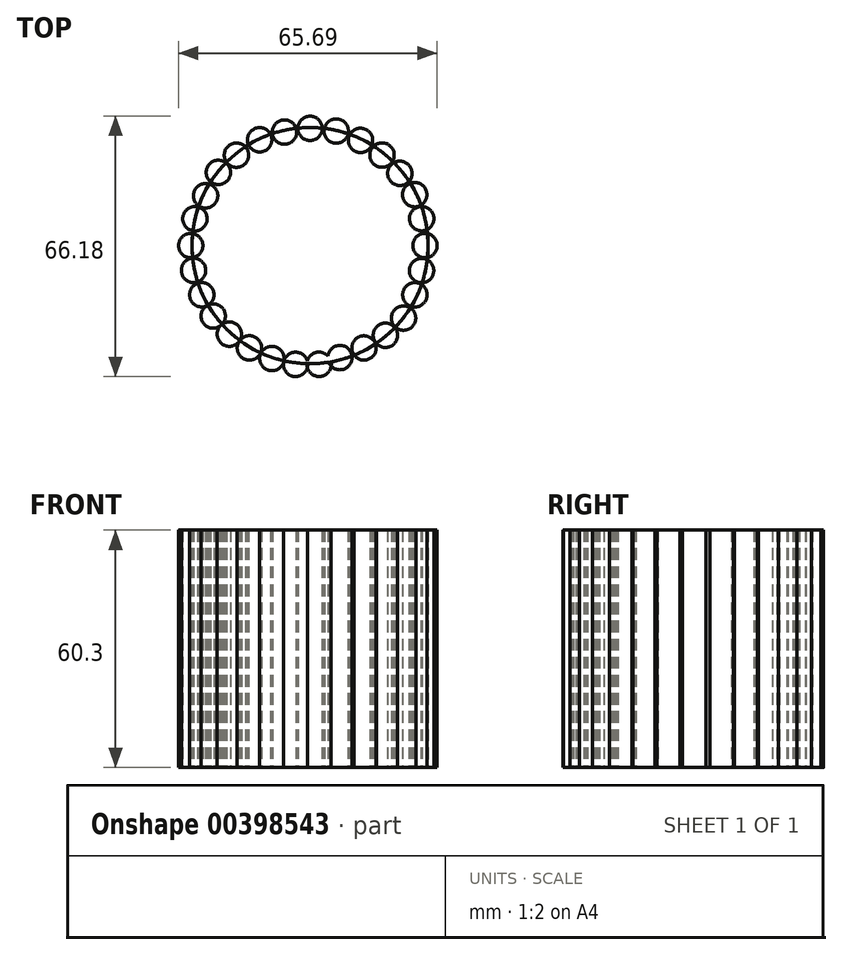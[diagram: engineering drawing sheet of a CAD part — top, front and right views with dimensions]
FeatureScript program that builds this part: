
annotation { "Feature Type Name" : "Feature", "Feature Type Description" : "" }
export const myFeature = defineFeature(function(context is Context, id is Id, definition is map)
    precondition{}
    {
        {
            var Q0;
            Q0=qCreatedBy(makeId("Top.planeOp"),FACE);
            var sketch = newSketch(context, id + "F0", { "sketchPlane" : qUnion([Q0])});
            skCircle(sketch, "E0", {"center": v(0, 0) * mm, "radius": 30 * mm});
            skSolve(sketch);
        }
        {
            var Q0;
            Q0=makeQuery(id+"F0.imprint","IMPRINT",FACE,{"disambiguationData":[TD([[makeQuery(id+"F0.imprint","IMPRINT",EDGE,{"derivedFrom":sQuery(id+"F0.wireOp",EDGE,"E0")}),1.0]])]});
            var sketch = newSketch(context, id + "F1", { "sketchPlane" : qUnion([Q0])});
            skCircle(sketch, "E1", {"center": v(-18.7, 22.97) * mm, "radius": 3.1 * mm});
            skCircle(sketch, "E2", {"center": v(-12.8, 26.88) * mm, "radius": 3.1 * mm});
            skCircle(sketch, "E3", {"center": v(-6.5, 28.84) * mm, "radius": 3.1 * mm});
            skCircle(sketch, "E4", {"center": v(0, 29.8) * mm, "radius": 3.1 * mm});
            skCircle(sketch, "E5", {"center": v(6.65, 29.1) * mm, "radius": 3.1 * mm});
            skCircle(sketch, "E6", {"center": v(12.83, 26.72) * mm, "radius": 3.1 * mm});
            skCircle(sketch, "E7", {"center": v(18.28, 23) * mm, "radius": 3.1 * mm});
            skCircle(sketch, "E8", {"center": v(22.82, 18.35) * mm, "radius": 3.1 * mm});
            skCircle(sketch, "E9", {"center": v(26.6, 12.94) * mm, "radius": 3.1 * mm});
            skCircle(sketch, "E10", {"center": v(28.36, 6.83) * mm, "radius": 3.1 * mm});
            skCircle(sketch, "E11", {"center": v(29.2, 0) * mm, "radius": 3.1 * mm});
            skCircle(sketch, "E12", {"center": v(28.34, -6.36) * mm, "radius": 3.1 * mm});
            skCircle(sketch, "E13", {"center": v(26.63, -12.5) * mm, "radius": 3.1 * mm});
            skCircle(sketch, "E14", {"center": v(23.77, -18.42) * mm, "radius": 3.1 * mm});
            skCircle(sketch, "E15", {"center": v(19.15, -22.78) * mm, "radius": 3.1 * mm});
            skCircle(sketch, "E16", {"center": v(-23.29, 18.6) * mm, "radius": 3.1 * mm});
            skCircle(sketch, "E17", {"center": v(-26.53, 12.65) * mm, "radius": 3.1 * mm});
            skCircle(sketch, "E18", {"center": v(-29.25, 6.82) * mm, "radius": 3.1 * mm});
            skCircle(sketch, "E19", {"center": v(-30.3, 0) * mm, "radius": 3.1 * mm});
            skCircle(sketch, "E20", {"center": v(-29.6, -6.3) * mm, "radius": 3.1 * mm});
            skCircle(sketch, "E21", {"center": v(-27.5, -12.5) * mm, "radius": 3.1 * mm});
            skCircle(sketch, "E22", {"center": v(-24.6, -17.9) * mm, "radius": 3.1 * mm});
            skCircle(sketch, "E23", {"center": v(-20.5, -22.5) * mm, "radius": 3.1 * mm});
            skCircle(sketch, "E24", {"center": v(13.7, -26) * mm, "radius": 3.1 * mm});
            skCircle(sketch, "E25", {"center": v(-15.4, -26) * mm, "radius": 3.1 * mm});
            skCircle(sketch, "E26", {"center": v(7.6, -28.46) * mm, "radius": 3.1 * mm});
            skCircle(sketch, "E27", {"center": v(-9.7, -28.7) * mm, "radius": 3.1 * mm});
            skCircle(sketch, "E28", {"center": v(-3.66, -30.18) * mm, "radius": 3.1 * mm});
            skCircle(sketch, "E29", {"center": v(2.3, -30.16) * mm, "radius": 3.1 * mm});
            skSolve(sketch);
        }
        {
            var Q0;
            {var subQ1=makeQuery(id+"F0.imprint","IMPRINT",EDGE,{"derivedFrom":sQuery(id+"F0.wireOp",EDGE,"E0")});var subQ36=sQuery(id+"F1.wireOp",EDGE,"E1");var subQ62=makeQuery(id+"F1.imprint","INTERSECT",VERTEX,{"disambiguationData":[OD(0.0)],"derivedFrom":[subQ1,subQ36]});Q0=makeQuery(id+"F1.imprint","IMPRINT",FACE,{"disambiguationData":[TD([[makeQuery(id+"F1.imprint","IMPRINT",EDGE,{"disambiguationData":[TD([[subQ62,-1.0]])],"derivedFrom":subQ36}),-1.0]])]});}
            var Q1;
            {var subQ0=sQuery(id+"F1.wireOp",EDGE,"E13");var subQ1=makeQuery(id+"F0.imprint","IMPRINT",EDGE,{"derivedFrom":sQuery(id+"F0.wireOp",EDGE,"E0")});var subQ2=makeQuery(id+"F1.imprint","INTERSECT",VERTEX,{"disambiguationData":[OD(0.0)],"derivedFrom":[subQ1,subQ0]});Q1=makeQuery(id+"F1.imprint","IMPRINT",FACE,{"disambiguationData":[TD([[makeQuery(id+"F1.imprint","IMPRINT",EDGE,{"disambiguationData":[TD([[subQ2,-1.0]])],"derivedFrom":subQ0}),1.0]])]});}
            var Q2;
            {var subQ0=sQuery(id+"F1.wireOp",EDGE,"E14");var subQ1=makeQuery(id+"F0.imprint","IMPRINT",EDGE,{"derivedFrom":sQuery(id+"F0.wireOp",EDGE,"E0")});var subQ2=makeQuery(id+"F1.imprint","INTERSECT",VERTEX,{"disambiguationData":[OD(0.0)],"derivedFrom":[subQ1,subQ0]});Q2=makeQuery(id+"F1.imprint","IMPRINT",FACE,{"disambiguationData":[TD([[makeQuery(id+"F1.imprint","IMPRINT",EDGE,{"disambiguationData":[TD([[subQ2,-1.0]])],"derivedFrom":subQ0}),1.0]])]});}
            var Q3;
            Q3=makeQuery(id+"F0.imprint","IMPRINT",FACE,{"disambiguationData":[TD([[makeQuery(id+"F0.imprint","IMPRINT",EDGE,{"derivedFrom":sQuery(id+"F0.wireOp",EDGE,"E0")}),1.0]])]});
            var Q4;
            {var subQ0=sQuery(id+"F1.wireOp",EDGE,"E12");var subQ1=makeQuery(id+"F0.imprint","IMPRINT",EDGE,{"derivedFrom":sQuery(id+"F0.wireOp",EDGE,"E0")});var subQ2=makeQuery(id+"F1.imprint","INTERSECT",VERTEX,{"disambiguationData":[OD(0.0)],"derivedFrom":[subQ1,subQ0]});Q4=makeQuery(id+"F1.imprint","IMPRINT",FACE,{"disambiguationData":[TD([[makeQuery(id+"F1.imprint","IMPRINT",EDGE,{"disambiguationData":[TD([[subQ2,-1.0]])],"derivedFrom":subQ0}),1.0]])]});}
            var Q5;
            {var subQ0=sQuery(id+"F1.wireOp",EDGE,"E11");var subQ1=makeQuery(id+"F0.imprint","IMPRINT",EDGE,{"derivedFrom":sQuery(id+"F0.wireOp",EDGE,"E0")});var subQ2=makeQuery(id+"F1.imprint","INTERSECT",VERTEX,{"disambiguationData":[OD(0.0)],"derivedFrom":[subQ1,subQ0]});Q5=makeQuery(id+"F1.imprint","IMPRINT",FACE,{"disambiguationData":[TD([[makeQuery(id+"F1.imprint","IMPRINT",EDGE,{"disambiguationData":[TD([[subQ2,-1.0]])],"derivedFrom":subQ0}),1.0]])]});}
            var Q6;
            {var subQ0=sQuery(id+"F1.wireOp",EDGE,"E10");var subQ1=makeQuery(id+"F0.imprint","IMPRINT",EDGE,{"derivedFrom":sQuery(id+"F0.wireOp",EDGE,"E0")});var subQ2=makeQuery(id+"F1.imprint","INTERSECT",VERTEX,{"disambiguationData":[OD(0.0)],"derivedFrom":[subQ1,subQ0]});Q6=makeQuery(id+"F1.imprint","IMPRINT",FACE,{"disambiguationData":[TD([[makeQuery(id+"F1.imprint","IMPRINT",EDGE,{"disambiguationData":[TD([[subQ2,-1.0]])],"derivedFrom":subQ0}),1.0]])]});}
            var Q7;
            {var subQ0=sQuery(id+"F1.wireOp",EDGE,"E9");var subQ1=makeQuery(id+"F0.imprint","IMPRINT",EDGE,{"derivedFrom":sQuery(id+"F0.wireOp",EDGE,"E0")});var subQ2=makeQuery(id+"F1.imprint","INTERSECT",VERTEX,{"disambiguationData":[OD(0.0)],"derivedFrom":[subQ1,subQ0]});Q7=makeQuery(id+"F1.imprint","IMPRINT",FACE,{"disambiguationData":[TD([[makeQuery(id+"F1.imprint","IMPRINT",EDGE,{"disambiguationData":[TD([[subQ2,-1.0]])],"derivedFrom":subQ0}),1.0]])]});}
            var Q8;
            {var subQ0=sQuery(id+"F1.wireOp",EDGE,"E8");var subQ1=makeQuery(id+"F0.imprint","IMPRINT",EDGE,{"derivedFrom":sQuery(id+"F0.wireOp",EDGE,"E0")});var subQ2=makeQuery(id+"F1.imprint","INTERSECT",VERTEX,{"disambiguationData":[OD(0.0)],"derivedFrom":[subQ1,subQ0]});Q8=makeQuery(id+"F1.imprint","IMPRINT",FACE,{"disambiguationData":[TD([[makeQuery(id+"F1.imprint","IMPRINT",EDGE,{"disambiguationData":[TD([[subQ2,-1.0]])],"derivedFrom":subQ0}),1.0]])]});}
            var Q9;
            {var subQ0=sQuery(id+"F1.wireOp",EDGE,"E7");var subQ1=makeQuery(id+"F0.imprint","IMPRINT",EDGE,{"derivedFrom":sQuery(id+"F0.wireOp",EDGE,"E0")});var subQ2=makeQuery(id+"F1.imprint","INTERSECT",VERTEX,{"disambiguationData":[OD(0.0)],"derivedFrom":[subQ1,subQ0]});Q9=makeQuery(id+"F1.imprint","IMPRINT",FACE,{"disambiguationData":[TD([[makeQuery(id+"F1.imprint","IMPRINT",EDGE,{"disambiguationData":[TD([[subQ2,-1.0]])],"derivedFrom":subQ0}),1.0]])]});}
            var Q10;
            {var subQ0=sQuery(id+"F1.wireOp",EDGE,"E6");var subQ1=makeQuery(id+"F0.imprint","IMPRINT",EDGE,{"derivedFrom":sQuery(id+"F0.wireOp",EDGE,"E0")});var subQ2=makeQuery(id+"F1.imprint","INTERSECT",VERTEX,{"disambiguationData":[OD(0.0)],"derivedFrom":[subQ1,subQ0]});Q10=makeQuery(id+"F1.imprint","IMPRINT",FACE,{"disambiguationData":[TD([[makeQuery(id+"F1.imprint","IMPRINT",EDGE,{"disambiguationData":[TD([[subQ2,1.0]])],"derivedFrom":subQ0}),1.0]])]});}
            var Q11;
            {var subQ0=sQuery(id+"F1.wireOp",EDGE,"E5");var subQ1=makeQuery(id+"F0.imprint","IMPRINT",EDGE,{"derivedFrom":sQuery(id+"F0.wireOp",EDGE,"E0")});var subQ2=makeQuery(id+"F1.imprint","INTERSECT",VERTEX,{"disambiguationData":[OD(0.0)],"derivedFrom":[subQ1,subQ0]});Q11=makeQuery(id+"F1.imprint","IMPRINT",FACE,{"disambiguationData":[TD([[makeQuery(id+"F1.imprint","IMPRINT",EDGE,{"disambiguationData":[TD([[subQ2,1.0]])],"derivedFrom":subQ0}),1.0]])]});}
            var Q12;
            {var subQ0=sQuery(id+"F1.wireOp",EDGE,"E4");var subQ1=makeQuery(id+"F0.imprint","IMPRINT",EDGE,{"derivedFrom":sQuery(id+"F0.wireOp",EDGE,"E0")});var subQ2=makeQuery(id+"F1.imprint","INTERSECT",VERTEX,{"disambiguationData":[OD(0.0)],"derivedFrom":[subQ1,subQ0]});Q12=makeQuery(id+"F1.imprint","IMPRINT",FACE,{"disambiguationData":[TD([[makeQuery(id+"F1.imprint","IMPRINT",EDGE,{"disambiguationData":[TD([[subQ2,1.0]])],"derivedFrom":subQ0}),1.0]])]});}
            var Q13;
            {var subQ0=sQuery(id+"F1.wireOp",EDGE,"E3");var subQ1=makeQuery(id+"F0.imprint","IMPRINT",EDGE,{"derivedFrom":sQuery(id+"F0.wireOp",EDGE,"E0")});var subQ2=makeQuery(id+"F1.imprint","INTERSECT",VERTEX,{"disambiguationData":[OD(0.0)],"derivedFrom":[subQ1,subQ0]});Q13=makeQuery(id+"F1.imprint","IMPRINT",FACE,{"disambiguationData":[TD([[makeQuery(id+"F1.imprint","IMPRINT",EDGE,{"disambiguationData":[TD([[subQ2,1.0]])],"derivedFrom":subQ0}),1.0]])]});}
            var Q14;
            {var subQ0=sQuery(id+"F1.wireOp",EDGE,"E2");var subQ1=makeQuery(id+"F0.imprint","IMPRINT",EDGE,{"derivedFrom":sQuery(id+"F0.wireOp",EDGE,"E0")});var subQ2=makeQuery(id+"F1.imprint","INTERSECT",VERTEX,{"disambiguationData":[OD(0.0)],"derivedFrom":[subQ1,subQ0]});Q14=makeQuery(id+"F1.imprint","IMPRINT",FACE,{"disambiguationData":[TD([[makeQuery(id+"F1.imprint","IMPRINT",EDGE,{"disambiguationData":[TD([[subQ2,1.0]])],"derivedFrom":subQ0}),1.0]])]});}
            var Q15;
            {var subQ0=sQuery(id+"F1.wireOp",EDGE,"E1");var subQ1=makeQuery(id+"F0.imprint","IMPRINT",EDGE,{"derivedFrom":sQuery(id+"F0.wireOp",EDGE,"E0")});var subQ2=makeQuery(id+"F1.imprint","INTERSECT",VERTEX,{"disambiguationData":[OD(0.0)],"derivedFrom":[subQ1,subQ0]});Q15=makeQuery(id+"F1.imprint","IMPRINT",FACE,{"disambiguationData":[TD([[makeQuery(id+"F1.imprint","IMPRINT",EDGE,{"disambiguationData":[TD([[subQ2,1.0]])],"derivedFrom":subQ0}),1.0]])]});}
            var Q16;
            {var subQ0=sQuery(id+"F1.wireOp",EDGE,"E16");var subQ1=makeQuery(id+"F0.imprint","IMPRINT",EDGE,{"derivedFrom":sQuery(id+"F0.wireOp",EDGE,"E0")});var subQ2=makeQuery(id+"F1.imprint","INTERSECT",VERTEX,{"disambiguationData":[OD(0.0)],"derivedFrom":[subQ1,subQ0]});Q16=makeQuery(id+"F1.imprint","IMPRINT",FACE,{"disambiguationData":[TD([[makeQuery(id+"F1.imprint","IMPRINT",EDGE,{"disambiguationData":[TD([[subQ2,1.0]])],"derivedFrom":subQ0}),1.0]])]});}
            var Q17;
            {var subQ0=sQuery(id+"F1.wireOp",EDGE,"E17");var subQ1=makeQuery(id+"F0.imprint","IMPRINT",EDGE,{"derivedFrom":sQuery(id+"F0.wireOp",EDGE,"E0")});var subQ2=makeQuery(id+"F1.imprint","INTERSECT",VERTEX,{"disambiguationData":[OD(0.0)],"derivedFrom":[subQ1,subQ0]});Q17=makeQuery(id+"F1.imprint","IMPRINT",FACE,{"disambiguationData":[TD([[makeQuery(id+"F1.imprint","IMPRINT",EDGE,{"disambiguationData":[TD([[subQ2,1.0]])],"derivedFrom":subQ0}),1.0]])]});}
            var Q18;
            {var subQ0=sQuery(id+"F1.wireOp",EDGE,"E18");var subQ1=makeQuery(id+"F0.imprint","IMPRINT",EDGE,{"derivedFrom":sQuery(id+"F0.wireOp",EDGE,"E0")});var subQ2=makeQuery(id+"F1.imprint","INTERSECT",VERTEX,{"disambiguationData":[OD(0.0)],"derivedFrom":[subQ1,subQ0]});Q18=makeQuery(id+"F1.imprint","IMPRINT",FACE,{"disambiguationData":[TD([[makeQuery(id+"F1.imprint","IMPRINT",EDGE,{"disambiguationData":[TD([[subQ2,1.0]])],"derivedFrom":subQ0}),1.0]])]});}
            var Q19;
            {var subQ0=sQuery(id+"F1.wireOp",EDGE,"E19");var subQ1=makeQuery(id+"F0.imprint","IMPRINT",EDGE,{"derivedFrom":sQuery(id+"F0.wireOp",EDGE,"E0")});var subQ2=makeQuery(id+"F1.imprint","INTERSECT",VERTEX,{"disambiguationData":[OD(0.0)],"derivedFrom":[subQ1,subQ0]});Q19=makeQuery(id+"F1.imprint","IMPRINT",FACE,{"disambiguationData":[TD([[makeQuery(id+"F1.imprint","IMPRINT",EDGE,{"disambiguationData":[TD([[subQ2,1.0]])],"derivedFrom":subQ0}),1.0]])]});}
            var Q20;
            {var subQ0=sQuery(id+"F1.wireOp",EDGE,"E20");var subQ1=makeQuery(id+"F0.imprint","IMPRINT",EDGE,{"derivedFrom":sQuery(id+"F0.wireOp",EDGE,"E0")});var subQ2=makeQuery(id+"F1.imprint","INTERSECT",VERTEX,{"disambiguationData":[OD(0.0)],"derivedFrom":[subQ1,subQ0]});Q20=makeQuery(id+"F1.imprint","IMPRINT",FACE,{"disambiguationData":[TD([[makeQuery(id+"F1.imprint","IMPRINT",EDGE,{"disambiguationData":[TD([[subQ2,1.0]])],"derivedFrom":subQ0}),1.0]])]});}
            var Q21;
            {var subQ0=sQuery(id+"F1.wireOp",EDGE,"E22");var subQ1=sQuery(id+"F1.wireOp",EDGE,"E21");var subQ2=makeQuery(id+"F1.imprint","INTERSECT",VERTEX,{"disambiguationData":[OD(0.0)],"derivedFrom":[subQ1,subQ0]});Q21=makeQuery(id+"F1.imprint","IMPRINT",FACE,{"disambiguationData":[TD([[makeQuery(id+"F1.imprint","IMPRINT",EDGE,{"disambiguationData":[TD([[subQ2,1.0]])],"derivedFrom":subQ1}),1.0]])]});}
            var Q22;
            {var subQ0=sQuery(id+"F1.wireOp",EDGE,"E22");var subQ1=sQuery(id+"F1.wireOp",EDGE,"E21");var subQ2=makeQuery(id+"F1.imprint","INTERSECT",VERTEX,{"disambiguationData":[OD(0.0)],"derivedFrom":[subQ1,subQ0]});Q22=makeQuery(id+"F1.imprint","IMPRINT",FACE,{"disambiguationData":[TD([[makeQuery(id+"F1.imprint","IMPRINT",EDGE,{"disambiguationData":[TD([[subQ2,-1.0]])],"derivedFrom":subQ1}),-1.0]])]});}
            var Q23;
            {var subQ0=sQuery(id+"F1.wireOp",EDGE,"E23");var subQ1=sQuery(id+"F1.wireOp",EDGE,"E22");var subQ2=makeQuery(id+"F1.imprint","INTERSECT",VERTEX,{"disambiguationData":[OD(0.0)],"derivedFrom":[subQ1,subQ0]});Q23=makeQuery(id+"F1.imprint","IMPRINT",FACE,{"disambiguationData":[TD([[makeQuery(id+"F1.imprint","IMPRINT",EDGE,{"disambiguationData":[TD([[subQ2,-1.0]])],"derivedFrom":subQ1}),-1.0]])]});}
            var Q24;
            {var subQ0=sQuery(id+"F1.wireOp",EDGE,"E25");var subQ1=sQuery(id+"F1.wireOp",EDGE,"E23");var subQ2=makeQuery(id+"F1.imprint","INTERSECT",VERTEX,{"disambiguationData":[OD(0.0)],"derivedFrom":[subQ1,subQ0]});Q24=makeQuery(id+"F1.imprint","IMPRINT",FACE,{"disambiguationData":[TD([[makeQuery(id+"F1.imprint","IMPRINT",EDGE,{"disambiguationData":[TD([[subQ2,-1.0]])],"derivedFrom":subQ1}),-1.0]])]});}
            var Q25;
            {var subQ0=sQuery(id+"F1.wireOp",EDGE,"E27");var subQ1=makeQuery(id+"F0.imprint","IMPRINT",EDGE,{"derivedFrom":sQuery(id+"F0.wireOp",EDGE,"E0")});var subQ2=makeQuery(id+"F1.imprint","INTERSECT",VERTEX,{"disambiguationData":[OD(0.0)],"derivedFrom":[subQ1,subQ0]});Q25=makeQuery(id+"F1.imprint","IMPRINT",FACE,{"disambiguationData":[TD([[makeQuery(id+"F1.imprint","IMPRINT",EDGE,{"disambiguationData":[TD([[subQ2,-1.0]])],"derivedFrom":subQ0}),1.0]])]});}
            var Q26;
            {var subQ0=sQuery(id+"F1.wireOp",EDGE,"E29");var subQ1=sQuery(id+"F1.wireOp",EDGE,"E28");var subQ2=makeQuery(id+"F1.imprint","INTERSECT",VERTEX,{"disambiguationData":[OD(0.0)],"derivedFrom":[subQ1,subQ0]});Q26=makeQuery(id+"F1.imprint","IMPRINT",FACE,{"disambiguationData":[TD([[makeQuery(id+"F1.imprint","IMPRINT",EDGE,{"disambiguationData":[TD([[subQ2,1.0]])],"derivedFrom":subQ1}),1.0]])]});}
            var Q27;
            {var subQ0=sQuery(id+"F1.wireOp",EDGE,"E29");var subQ1=sQuery(id+"F1.wireOp",EDGE,"E26");var subQ2=makeQuery(id+"F1.imprint","INTERSECT",VERTEX,{"disambiguationData":[OD(0.0)],"derivedFrom":[subQ1,subQ0]});Q27=makeQuery(id+"F1.imprint","IMPRINT",FACE,{"disambiguationData":[TD([[makeQuery(id+"F1.imprint","IMPRINT",EDGE,{"disambiguationData":[TD([[subQ2,1.0]])],"derivedFrom":subQ1}),-1.0]])]});}
            var Q28;
            {var subQ0=sQuery(id+"F1.wireOp",EDGE,"E29");var subQ1=sQuery(id+"F1.wireOp",EDGE,"E26");var subQ2=makeQuery(id+"F1.imprint","INTERSECT",VERTEX,{"disambiguationData":[OD(0.0)],"derivedFrom":[subQ1,subQ0]});Q28=makeQuery(id+"F1.imprint","IMPRINT",FACE,{"disambiguationData":[TD([[makeQuery(id+"F1.imprint","IMPRINT",EDGE,{"disambiguationData":[TD([[subQ2,-1.0]])],"derivedFrom":subQ1}),1.0]])]});}
            var Q29;
            {var subQ0=sQuery(id+"F1.wireOp",EDGE,"E24");var subQ1=makeQuery(id+"F0.imprint","IMPRINT",EDGE,{"derivedFrom":sQuery(id+"F0.wireOp",EDGE,"E0")});var subQ2=makeQuery(id+"F1.imprint","INTERSECT",VERTEX,{"disambiguationData":[OD(0.0)],"derivedFrom":[subQ1,subQ0]});Q29=makeQuery(id+"F1.imprint","IMPRINT",FACE,{"disambiguationData":[TD([[makeQuery(id+"F1.imprint","IMPRINT",EDGE,{"disambiguationData":[TD([[subQ2,-1.0]])],"derivedFrom":subQ0}),1.0]])]});}
            var Q30;
            {var subQ0=sQuery(id+"F1.wireOp",EDGE,"E15");var subQ1=makeQuery(id+"F0.imprint","IMPRINT",EDGE,{"derivedFrom":sQuery(id+"F0.wireOp",EDGE,"E0")});var subQ2=makeQuery(id+"F1.imprint","INTERSECT",VERTEX,{"disambiguationData":[OD(0.0)],"derivedFrom":[subQ1,subQ0]});Q30=makeQuery(id+"F1.imprint","IMPRINT",FACE,{"disambiguationData":[TD([[makeQuery(id+"F1.imprint","IMPRINT",EDGE,{"disambiguationData":[TD([[subQ2,-1.0]])],"derivedFrom":subQ0}),1.0]])]});}
            extrude(context, id + "F2", {"entities" : qUnion([Q0, Q1, Q2, Q3, Q4, Q5, Q6, Q7, Q8, Q9, Q10, Q11, Q12, Q13, Q14, Q15, Q16, Q17, Q18, Q19, Q20, Q21, Q22, Q23, Q24, Q25, Q26, Q27, Q28, Q29, Q30]), "depth" : 60.3 * mm});
        }
    });
